# Revit family: PH
name_source: partatom
category: Communication Devices
revit_build: Autodesk Revit 2014 (Build: 20130308_1515(x64)
units: mm (PartAtom-declared; Revit-internal decimal feet)

## types (1)
- PH
    Assembly Code = D5090
    Certifications = UL: E48166
2.4GHz Version - FCC: U.S. FCC Part 15.247 Class A: OUR-XBEE / OUR-XBEE PRO, Canada IC: 4214A-XBEE / 4214A-XBEE
PRO, Europe CE: ETSI / ETSI
900MHz Version - FCC: U.S. FCC Part 15.247 Class A: MCQ-XB900HP
UL94V-0 Flame retardant ABS or epoxy molding
    Default Elevation = 48 "
    Description = The Hubbell Control Solutions' (HCS) PowerHUBB nodes provide power distribution architecture and data connectivity to create a fully functioning Power over Ethernet (PoE) lighting control system. The PowerHUBB nodes implement a simplistic solution to controls by replacing the driver component and distributing direct control to the luminaire, achieving optimized power consumption.Programming is performed using the Gateway software, which communicates bi-directionally over a CAT5e/6 Cable that connects directly to the PowerHUBB node. Master Nodes receive data and power from the PoE network switch. These nodes then pass along the power and data downstream to any daisy-chained Satellite node(s). Connected nodes/luminaires are automatically discovered by the Gateway, expediting commissioning and administering immediate feedback. Each Master node is DHCP-enabled and will automatically receive an IP address from the local network to simplify installation and setup.
    Feartures = • Replaces standard electronic AC driver in luminaire
• Capable of Tunable White utilizing a 2-channel LED Board
• Programmed for optimized performance of LED
• Bi-directional communication
• Node is discovered immediately by Gateway software
• Low voltage inputs for control devices
• Provides dimming function down to 1%
• Direct connection to PSE device (PoE switch or midspan)
• DHCP-enabled
• Suitable for indoor applications
• Class 2 electrical device
• Plenum Rated
• UL924 listed
• Made in the USA
    Green = Plastic, Gray
    Housing Material = Paint - Hubbell - Carbon Black
    Manufacturer = Hubbell Control Solutions
    Model = PowerHUBB Nodes
    Product Documentation Link = https://hubbellcdn.com
    Product Page URL = https://www.hubbell.com
    Red = Paint - Hubbell - Red
    Type Comments = PowerHUBB™ Nodes
    URL = https://www.hubbell.com
    Warranty = 5-Years Warranty
    Yellow = Metal-Hubbell-Galvanized_Steel

## geometry (parser evidence)
native form markers: Sweep x3
no freeform markers — native parametric forms only
